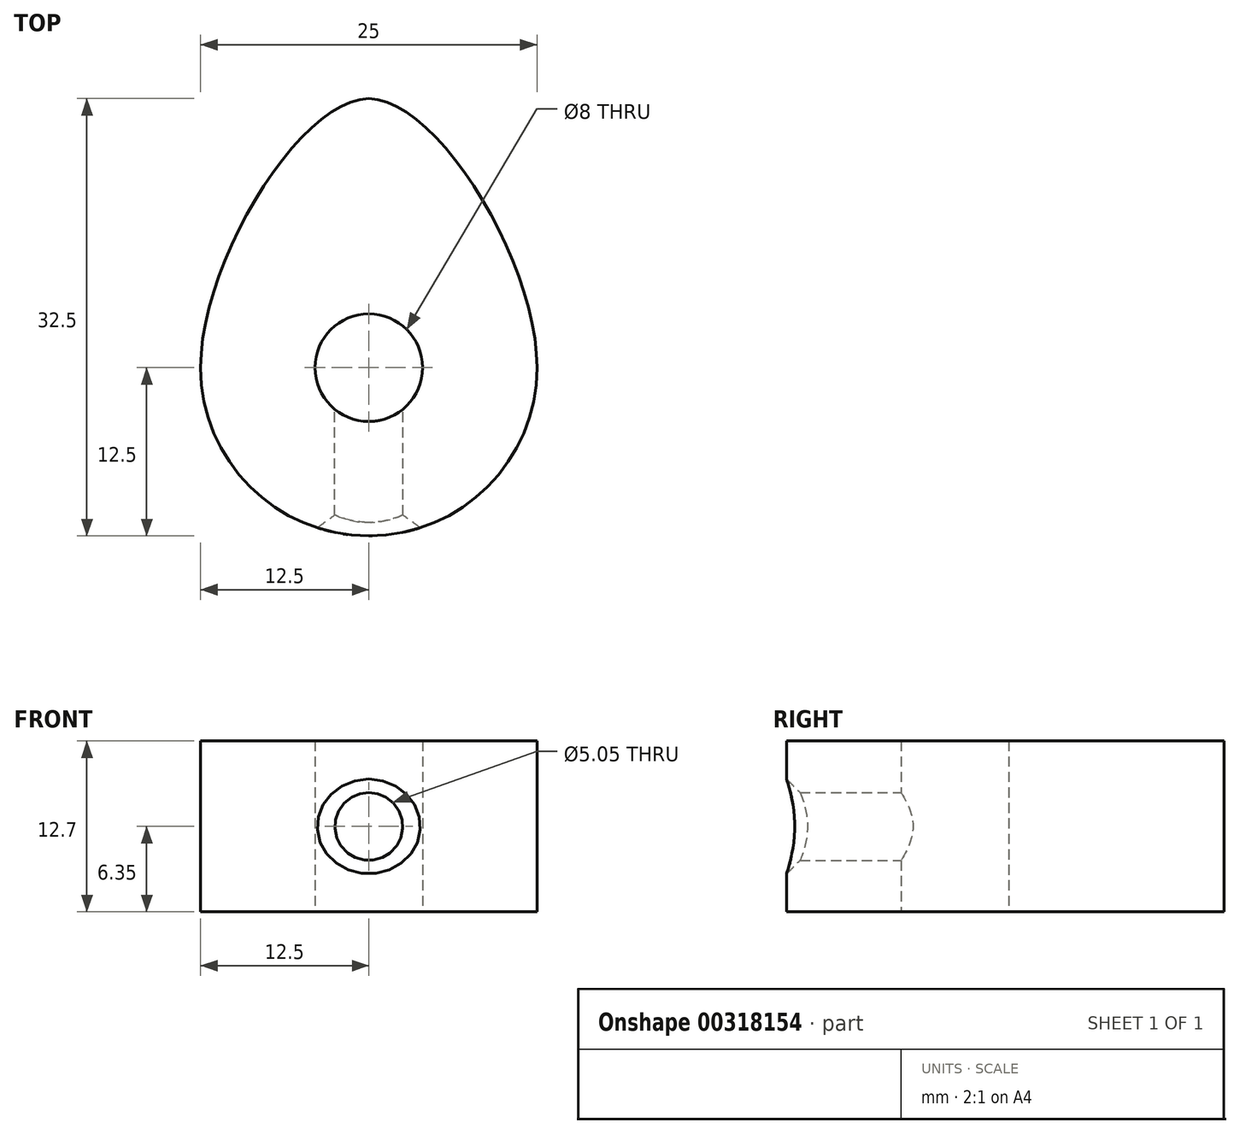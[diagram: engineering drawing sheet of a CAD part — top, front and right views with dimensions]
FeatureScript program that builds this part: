
annotation { "Feature Type Name" : "Feature", "Feature Type Description" : "" }
export const myFeature = defineFeature(function(context is Context, id is Id, definition is map)
    precondition{}
    {
        {
            var Q0;
            Q0=qCreatedBy(makeId("Top.planeOp"),FACE);
            var sketch = newSketch(context, id + "F0", { "sketchPlane" : qUnion([Q0])});
            skLineSegment(sketch, "E0", {"start": v(0, 0) * mm, "end": v(0, 20) * mm, "construction": true});
            skFitSpline(sketch, "E1", {"points": [v(0, 20) * mm, v(12.5, 0) * mm], "startDerivative": vector(15, 0) * mm, "endDerivative": vector(0, -24) * mm});
            skLineSegment(sketch, "E2", {"start": v(0, 0) * mm, "end": v(0, -12.5) * mm, "construction": true});
            skArc(sketch, "E3", {"start": v(0, -12.5) * mm, "mid": v(12.5, 0) * mm, "end": v(0, 12.5) * mm});
            skArc(sketch, "E4", {"start": v(0, -4) * mm, "mid": v(4, 0) * mm, "end": v(0, 4) * mm});
            skFitSpline(sketch, "E5.MirrorCS", {"points": [v(0, 20) * mm, v(-12.5, 0) * mm], "startDerivative": vector(-15, 0) * mm, "endDerivative": vector(0, -24) * mm});
            skArc(sketch, "E6.MirrorCS", {"start": v(0, -12.5) * mm, "mid": v(-12.5, 0) * mm, "end": v(0, 12.5) * mm});
            skArc(sketch, "E7.MirrorCS", {"start": v(0, -4) * mm, "mid": v(-4, 0) * mm, "end": v(0, 4) * mm});
            skSolve(sketch);
        }
        {
            var Q0;
            {var subQ0=sQuery(id+"F0.wireOp",EDGE,"E1");Q0=makeQuery(id+"F0.imprint","IMPRINT",FACE,{"disambiguationData":[TD([[makeQuery(id+"F0.imprint","IMPRINT",EDGE,{"derivedFrom":subQ0}),-1.0]])]});}
            var Q1;
            Q1=makeQuery(id+"F0.imprint","IMPRINT",FACE,{"disambiguationData":[TD([[makeQuery(id+"F0.imprint","IMPRINT",EDGE,{"derivedFrom":sQuery(id+"F0.wireOp",EDGE,"E4")}),-1.0]])]});
            extrude(context, id + "F1", {"entities" : qUnion([Q0, Q1]), "depth" : 12.7 * mm});
        }
        {
            var Q0;
            Q0=qCreatedBy(makeId("Front.planeOp"),FACE);
            var sketch = newSketch(context, id + "F2", { "sketchPlane" : qUnion([Q0])});
            skLineSegment(sketch, "E8.0.0", {"start": v(-12.5, 0) * mm, "end": v(12.5, 0) * mm});
            skLineSegment(sketch, "E8.0.1", {"start": v(12.5, 0) * mm, "end": v(12.5, 12.7) * mm});
            skLineSegment(sketch, "E8.0.2", {"start": v(12.5, 12.7) * mm, "end": v(-12.5, 12.7) * mm});
            skLineSegment(sketch, "E8.0.3", {"start": v(-12.5, 12.7) * mm, "end": v(-12.5, 0) * mm});
            skCircle(sketch, "E9", {"center": v(0, 6.35) * mm, "radius": 2.52 * mm});
            skLineSegment(sketch, "E10", {"start": v(-12.5, 12.7) * mm, "end": v(12.5, 0) * mm, "construction": true});
            skSolve(sketch);
        }
        {
            var Q0;
            Q0=makeQuery(id+"F2.imprint","IMPRINT",FACE,{"disambiguationData":[TD([[makeQuery(id+"F2.imprint","IMPRINT",EDGE,{"derivedFrom":sQuery(id+"F2.wireOp",EDGE,"E9")}),1.0]])]});
            extrude(context, id + "F3", {"entities" : qUnion([Q0]), "operationType" : NewBodyOperationType.REMOVE, "endBound" : BoundingType.THROUGH_ALL, "depth" : 25 * mm});
        }
        {
            var Q0;
            Q0=makeQuery(id+"F3.boolean.opBoolean","INTERSECT",EDGE,{"derivedFrom":[makeQuery(id+"F1.opExtrude","SWEPT_FACE",FACE,{"disambiguationData":[OSD([sQuery(id+"F0.wireOp",EDGE,"E3"),sQuery(id+"F0.wireOp",EDGE,"E6.MirrorCS")])]}),makeQuery(id+"F3.opExtrude","SWEPT_FACE",FACE,{"disambiguationData":[OSD([sQuery(id+"F2.wireOp",EDGE,"E9")])]})]});
            chamfer(context, id + "F4", {"entities" : qUnion([Q0]), "width" : 1 * mm, "tangentPropagation" : true});
        }
    });
